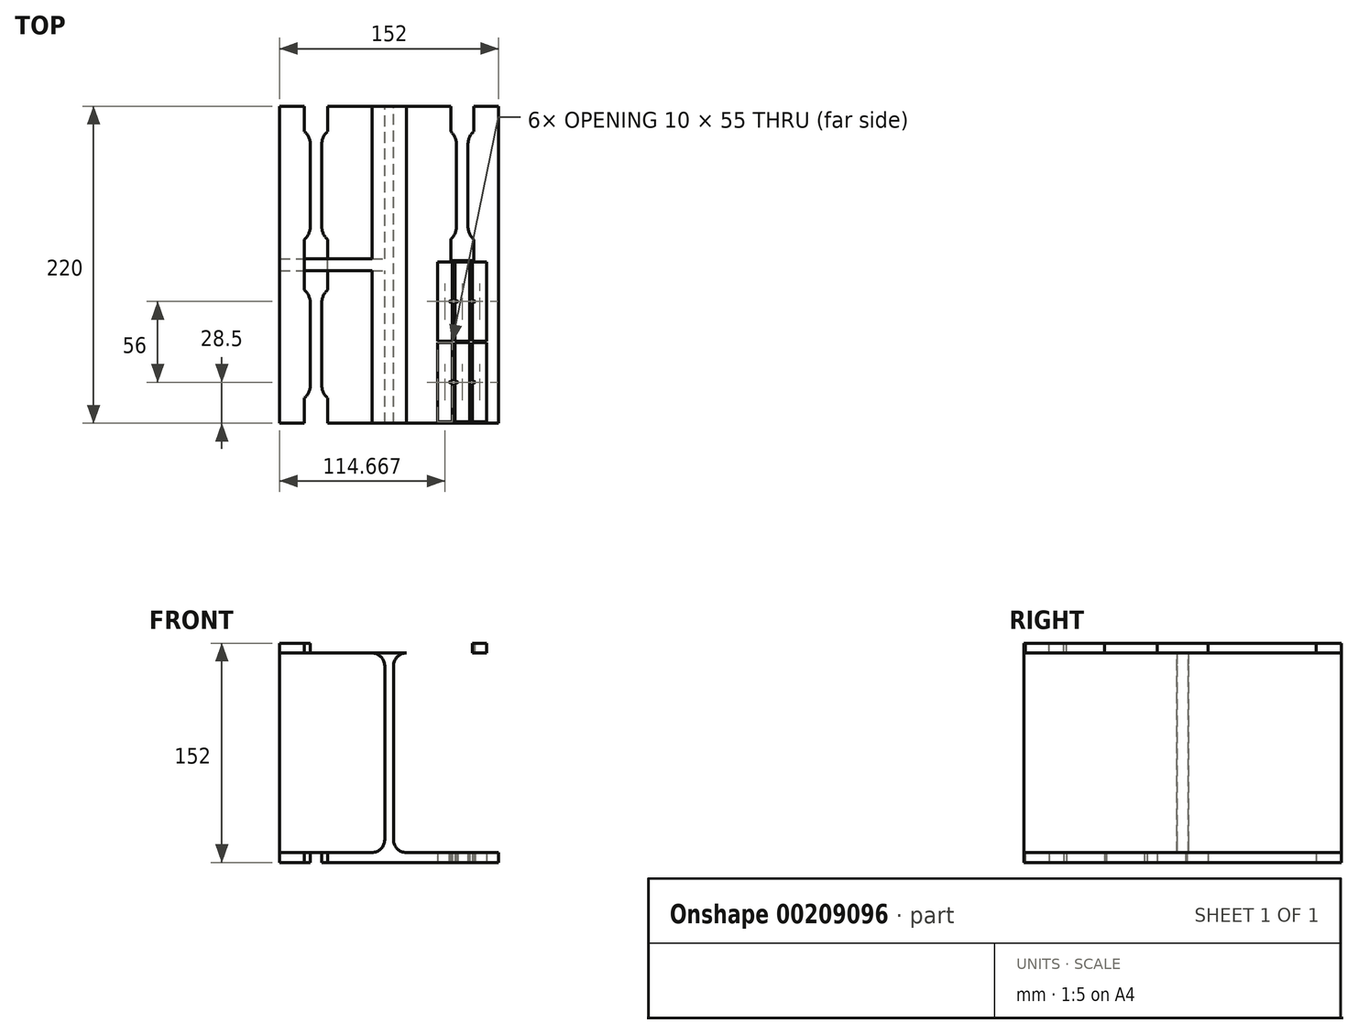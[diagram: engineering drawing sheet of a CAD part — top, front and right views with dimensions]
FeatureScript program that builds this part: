
annotation { "Feature Type Name" : "Feature", "Feature Type Description" : "" }
export const myFeature = defineFeature(function(context is Context, id is Id, definition is map)
    precondition{}
    {
        {
            var Q0;
            Q0=qCreatedBy(makeId("Front.planeOp"),FACE);
            var sketch = newSketch(context, id + "F0", { "sketchPlane" : qUnion([Q0])});
            skLineSegment(sketch, "E0.left", {"start": v(3.05, -60.3) * mm, "end": v(3.05, 60.3) * mm});
            skLineSegment(sketch, "E0.right", {"start": v(-3.05, -60.3) * mm, "end": v(-3.05, 60.3) * mm});
            skPoint(sketch, "E0.middle", {"position": v(0, 0) * mm});
            skLineSegment(sketch, "E1.top", {"start": v(76, 76) * mm, "end": v(-76, 76) * mm});
            skLineSegment(sketch, "E1.left", {"start": v(76, 69.2) * mm, "end": v(76, 76) * mm});
            skLineSegment(sketch, "E1.right", {"start": v(-76, 69.2) * mm, "end": v(-76, 76) * mm});
            skPoint(sketch, "E1.middle", {"position": v(0, 72.6) * mm});
            skPoint(sketch, "E1.middle.positionSnap0", {"position": v(0, 69.2) * mm});
            skPoint(sketch, "E1.centerSnap0", {"position": v(0, 69.2) * mm});
            skLineSegment(sketch, "E2.top", {"start": v(76, -76) * mm, "end": v(-76, -76) * mm});
            skLineSegment(sketch, "E2.left", {"start": v(76, -69.2) * mm, "end": v(76, -76) * mm});
            skLineSegment(sketch, "E2.right", {"start": v(-76, -69.2) * mm, "end": v(-76, -76) * mm});
            skPoint(sketch, "E2.middle", {"position": v(0, -72.6) * mm});
            skLineSegment(sketch, "E3", {"start": v(-76, 69.2) * mm, "end": v(-11.95, 69.2) * mm});
            skLineSegment(sketch, "E4", {"start": v(11.95, 69.2) * mm, "end": v(76, 69.2) * mm});
            skLineSegment(sketch, "E5", {"start": v(11.95, -69.2) * mm, "end": v(76, -69.2) * mm});
            skLineSegment(sketch, "E6", {"start": v(-11.95, -69.2) * mm, "end": v(-76, -69.2) * mm});
            skPoint(sketch, "E7.visualSharp", {"position": v(-3.05, 69.2) * mm});
            skArc(sketch, "E7.filletArc", {"start": v(-3.05, 60.3) * mm, "mid": v(-5.66, 66.6) * mm, "end": v(-11.95, 69.2) * mm});
            skPoint(sketch, "E8.visualSharp", {"position": v(3.05, 69.2) * mm});
            skArc(sketch, "E8.filletArc", {"start": v(11.95, 69.2) * mm, "mid": v(5.66, 66.6) * mm, "end": v(3.05, 60.3) * mm});
            skPoint(sketch, "E9.visualSharp", {"position": v(-3.05, -69.2) * mm});
            skArc(sketch, "E9.filletArc", {"start": v(-11.95, -69.2) * mm, "mid": v(-5.66, -66.6) * mm, "end": v(-3.05, -60.3) * mm});
            skPoint(sketch, "E10.visualSharp", {"position": v(3.05, -69.2) * mm});
            skArc(sketch, "E10.filletArc", {"start": v(3.05, -60.3) * mm, "mid": v(5.66, -66.6) * mm, "end": v(11.95, -69.2) * mm});
            skPoint(sketch, "E11.startSnap0", {"position": v(-5.66, 66.6) * mm});
            skPoint(sketch, "E11.endSnap0", {"position": v(-5.66, 66.6) * mm});
            skPoint(sketch, "E12.startSnap0", {"position": v(-5.66, -66.6) * mm});
            skSolve(sketch);
        }
        {
            var Q0;
            Q0=makeQuery(id+"F0.imprint","IMPRINT",FACE,{"disambiguationData":[TD([[makeQuery(id+"F0.imprint","IMPRINT",EDGE,{"derivedFrom":sQuery(id+"F0.wireOp",EDGE,"E0.left")}),1.0]])]});
            extrude(context, id + "F1", {"entities" : qUnion([Q0]), "depth" : 220 * mm, "symmetric" : true});
        }
        {
            var Q0;
            Q0=makeQuery(id+"F1.opExtrude","SWEPT_FACE",FACE,{"disambiguationData":[OSD([sQuery(id+"F0.wireOp",EDGE,"E1.top")])]});
            var sketch = newSketch(context, id + "F2", { "sketchPlane" : qUnion([Q0])});
            skLineSegment(sketch, "E13.bottom", {"start": v(0, -4) * mm, "end": v(-76, -4) * mm});
            skLineSegment(sketch, "E13.top", {"start": v(0, 4) * mm, "end": v(-76, 4) * mm});
            skLineSegment(sketch, "E13.left", {"start": v(0, -4) * mm, "end": v(0, 4) * mm});
            skLineSegment(sketch, "E13.right", {"start": v(-76, -4) * mm, "end": v(-76, 4) * mm});
            skPoint(sketch, "E13.middle", {"position": v(-38, 0) * mm});
            skSolve(sketch);
        }
        {
            var Q0;
            Q0=makeQuery(id+"F2.imprint","IMPRINT",FACE,{"disambiguationData":[TD([[makeQuery(id+"F2.imprint","IMPRINT",EDGE,{"derivedFrom":sQuery(id+"F2.wireOp",EDGE,"E13.bottom")}),-1.0]])]});
            extrude(context, id + "F3", {"entities" : qUnion([Q0]), "operationType" : NewBodyOperationType.ADD, "oppositeDirection" : true, "depth" : 152 * mm});
        }
        {
            var Q0;
            Q0=makeQuery(id+"F1.opExtrude","SWEPT_FACE",FACE,{"disambiguationData":[OSD([sQuery(id+"F0.wireOp",EDGE,"E1.top")])]});
            var sketch = newSketch(context, id + "F4", { "sketchPlane" : qUnion([Q0])});
            skLineSegment(sketch, "E14.bottom", {"start": v(58.67, 110) * mm, "end": v(42.67, 110) * mm});
            skPoint(sketch, "E14.middle", {"position": v(50.67, 55) * mm});
            skLineSegment(sketch, "E15.left", {"start": v(54.67, 26.5) * mm, "end": v(54.67, 83.5) * mm});
            skLineSegment(sketch, "E15.right", {"start": v(46.67, 26.5) * mm, "end": v(46.67, 83.5) * mm});
            skArc(sketch, "E16", {"start": v(54.67, 83.5) * mm, "mid": v(55.71, 88.4) * mm, "end": v(58.67, 92.44) * mm});
            skArc(sketch, "E17", {"start": v(46.67, 83.5) * mm, "mid": v(45.62, 88.4) * mm, "end": v(42.67, 92.44) * mm});
            skArc(sketch, "E18", {"start": v(54.67, 26.5) * mm, "mid": v(55.71, 21.6) * mm, "end": v(58.67, 17.56) * mm});
            skArc(sketch, "E19", {"start": v(46.67, 26.5) * mm, "mid": v(45.62, 21.6) * mm, "end": v(42.67, 17.56) * mm});
            skLineSegment(sketch, "E20", {"start": v(42.67, 92.44) * mm, "end": v(42.67, 110) * mm});
            skLineSegment(sketch, "E21", {"start": v(58.67, 110) * mm, "end": v(58.67, 92.44) * mm});
            skLineSegment(sketch, "E22", {"start": v(0, 116.32) * mm, "end": v(0, 123.72) * mm});
            skPoint(sketch, "E23.MirrorP", {"position": v(-50.67, 55) * mm});
            skLineSegment(sketch, "E24.MirrorCS", {"start": v(-58.67, 110) * mm, "end": v(-42.67, 110) * mm});
            skLineSegment(sketch, "E25.MirrorCS", {"start": v(-58.67, 110) * mm, "end": v(-58.67, 92.44) * mm});
            skLineSegment(sketch, "E26.MirrorCS", {"start": v(-42.67, 92.44) * mm, "end": v(-42.67, 110) * mm});
            skArc(sketch, "E27.MirrorCS", {"start": v(-54.67, 83.5) * mm, "mid": v(-55.71, 88.4) * mm, "end": v(-58.67, 92.44) * mm});
            skArc(sketch, "E28.MirrorCS", {"start": v(-46.67, 83.5) * mm, "mid": v(-45.62, 88.4) * mm, "end": v(-42.67, 92.44) * mm});
            skLineSegment(sketch, "E29.MirrorCS", {"start": v(-54.67, 26.5) * mm, "end": v(-54.67, 83.5) * mm});
            skLineSegment(sketch, "E30.MirrorCS", {"start": v(-46.67, 26.5) * mm, "end": v(-46.67, 83.5) * mm});
            skArc(sketch, "E31.MirrorCS", {"start": v(-54.67, 26.5) * mm, "mid": v(-55.71, 21.6) * mm, "end": v(-58.67, 17.56) * mm});
            skArc(sketch, "E32.MirrorCS", {"start": v(-46.67, 26.5) * mm, "mid": v(-45.62, 21.6) * mm, "end": v(-42.67, 17.56) * mm});
            skLineSegment(sketch, "E33.MirrorCS", {"start": v(-58.67, 0) * mm, "end": v(-58.67, 17.56) * mm});
            skLineSegment(sketch, "E34.MirrorCS", {"start": v(-58.67, 0) * mm, "end": v(-42.67, 0) * mm});
            skLineSegment(sketch, "E35.MirrorCS", {"start": v(-42.67, 17.56) * mm, "end": v(-42.67, 0) * mm});
            skPoint(sketch, "E36.MirrorP", {"position": v(-50.67, -55) * mm});
            skLineSegment(sketch, "E37.MirrorCS", {"start": v(-58.67, -110) * mm, "end": v(-42.67, -110) * mm});
            skLineSegment(sketch, "E38.MirrorCS", {"start": v(-42.67, -92.44) * mm, "end": v(-42.67, -110) * mm});
            skLineSegment(sketch, "E39.MirrorCS", {"start": v(-58.67, -110) * mm, "end": v(-58.67, -92.44) * mm});
            skArc(sketch, "E40.MirrorCS", {"start": v(-46.67, -83.5) * mm, "mid": v(-45.62, -88.4) * mm, "end": v(-42.67, -92.44) * mm});
            skArc(sketch, "E41.MirrorCS", {"start": v(-54.67, -83.5) * mm, "mid": v(-55.71, -88.4) * mm, "end": v(-58.67, -92.44) * mm});
            skLineSegment(sketch, "E42.MirrorCS", {"start": v(-46.67, -26.5) * mm, "end": v(-46.67, -83.5) * mm});
            skLineSegment(sketch, "E43.MirrorCS", {"start": v(-54.67, -26.5) * mm, "end": v(-54.67, -83.5) * mm});
            skArc(sketch, "E44.MirrorCS", {"start": v(-46.67, -26.5) * mm, "mid": v(-45.62, -21.6) * mm, "end": v(-42.67, -17.56) * mm});
            skArc(sketch, "E45.MirrorCS", {"start": v(-54.67, -26.5) * mm, "mid": v(-55.71, -21.6) * mm, "end": v(-58.67, -17.56) * mm});
            skLineSegment(sketch, "E46.MirrorCS", {"start": v(-42.67, -17.56) * mm, "end": v(-42.67, 0) * mm});
            skLineSegment(sketch, "E47.MirrorCS", {"start": v(-58.67, 0) * mm, "end": v(-58.67, -17.56) * mm});
            skLineSegment(sketch, "E48.bottom", {"start": v(55.67, 2) * mm, "end": v(45.67, 2) * mm});
            skLineSegment(sketch, "E48.top", {"start": v(55.67, -53) * mm, "end": v(45.67, -53) * mm});
            skLineSegment(sketch, "E48.left", {"start": v(55.67, 2) * mm, "end": v(55.67, -53) * mm});
            skPoint(sketch, "E48.middle", {"position": v(50.67, -25.5) * mm});
            skLineSegment(sketch, "E49.top", {"start": v(58.67, 3) * mm, "end": v(42.67, 3) * mm});
            skLineSegment(sketch, "E49.left", {"start": v(58.67, 17.56) * mm, "end": v(58.67, 3) * mm});
            skLineSegment(sketch, "E49.right", {"start": v(42.67, 17.56) * mm, "end": v(42.67, 3) * mm});
            skPoint(sketch, "E49.middle", {"position": v(50.67, 10.28) * mm});
            skLineSegment(sketch, "E50", {"start": v(47.51, -25.27) * mm, "end": v(45.67, -24.5) * mm});
            skLineSegment(sketch, "E51", {"start": v(47.51, -25.73) * mm, "end": v(45.67, -26.5) * mm});
            skLineSegment(sketch, "E52", {"start": v(42.27, -25.5) * mm, "end": v(40.71, -25.5) * mm});
            skPoint(sketch, "E52.startSnap0", {"position": v(45.67, -25.5) * mm});
            skPoint(sketch, "E53.visualSharp", {"position": v(48.07, -25.5) * mm});
            skArc(sketch, "E53.filletArc", {"start": v(47.51, -25.73) * mm, "mid": v(47.67, -25.5) * mm, "end": v(47.51, -25.27) * mm});
            skLineSegment(sketch, "E54", {"start": v(56.67, -9.9) * mm, "end": v(56.67, -20.52) * mm});
            skLineSegment(sketch, "E55", {"start": v(50.67, -17.9) * mm, "end": v(50.67, -13.5) * mm});
            skLineSegment(sketch, "E56.MirrorCS", {"start": v(44.67, -9.9) * mm, "end": v(44.67, -20.52) * mm});
            skLineSegment(sketch, "E57.MirrorCS", {"start": v(57.67, 2) * mm, "end": v(67.67, 2) * mm});
            skPoint(sketch, "E58.MirrorP", {"position": v(62.67, -25.5) * mm});
            skLineSegment(sketch, "E59.MirrorCS", {"start": v(57.67, -53) * mm, "end": v(67.67, -53) * mm});
            skLineSegment(sketch, "E60.MirrorCS", {"start": v(67.67, 2) * mm, "end": v(67.67, -53) * mm});
            skArc(sketch, "E61.MirrorCS", {"start": v(41.82, -25.73) * mm, "mid": v(41.67, -25.5) * mm, "end": v(41.82, -25.27) * mm});
            skLineSegment(sketch, "E62.MirrorCS", {"start": v(41.82, -25.27) * mm, "end": v(43.67, -24.5) * mm});
            skLineSegment(sketch, "E63.MirrorCS", {"start": v(41.82, -25.73) * mm, "end": v(43.67, -26.5) * mm});
            skLineSegment(sketch, "E64.MirrorCS", {"start": v(33.67, 2) * mm, "end": v(43.67, 2) * mm});
            skLineSegment(sketch, "E65.MirrorCS", {"start": v(38.67, -17.9) * mm, "end": v(38.67, -13.5) * mm});
            skPoint(sketch, "E66.MirrorP", {"position": v(38.67, -25.5) * mm});
            skPoint(sketch, "E67.MirrorP", {"position": v(43.67, -25.5) * mm});
            skLineSegment(sketch, "E68.MirrorCS", {"start": v(33.67, 2) * mm, "end": v(33.67, -53) * mm});
            skLineSegment(sketch, "E69.MirrorCS", {"start": v(33.67, -53) * mm, "end": v(43.67, -53) * mm});
            skPoint(sketch, "E70.MirrorP", {"position": v(41.26, -25.5) * mm});
            skLineSegment(sketch, "E71", {"start": v(62.67, -21.23) * mm, "end": v(62.67, -17.56) * mm});
            skArc(sketch, "E72.MirrorCS", {"start": v(59.51, -25.73) * mm, "mid": v(59.67, -25.5) * mm, "end": v(59.51, -25.27) * mm});
            skLineSegment(sketch, "E73.MirrorCS", {"start": v(59.51, -25.73) * mm, "end": v(57.67, -26.5) * mm});
            skLineSegment(sketch, "E74.MirrorCS", {"start": v(59.51, -25.27) * mm, "end": v(57.67, -24.5) * mm});
            skPoint(sketch, "E75.MirrorP", {"position": v(57.67, -25.5) * mm});
            skPoint(sketch, "E76.MirrorP", {"position": v(60.07, -25.5) * mm});
            skLineSegment(sketch, "E77", {"start": v(43.67, 2) * mm, "end": v(43.67, -24.5) * mm});
            skLineSegment(sketch, "E78", {"start": v(43.67, -26.5) * mm, "end": v(43.67, -53) * mm});
            skLineSegment(sketch, "E79", {"start": v(45.67, -53) * mm, "end": v(45.67, -26.5) * mm});
            skLineSegment(sketch, "E80", {"start": v(45.67, -24.5) * mm, "end": v(45.67, 2) * mm});
            skLineSegment(sketch, "E81", {"start": v(57.67, 2) * mm, "end": v(57.67, -24.5) * mm});
            skLineSegment(sketch, "E82", {"start": v(57.67, -26.5) * mm, "end": v(57.67, -53) * mm});
            skLineSegment(sketch, "E83", {"start": v(42.84, -53.5) * mm, "end": v(60.64, -53.5) * mm});
            skArc(sketch, "E84.MirrorCS", {"start": v(41.82, -81.27) * mm, "mid": v(41.67, -81.5) * mm, "end": v(41.82, -81.73) * mm});
            skLineSegment(sketch, "E85.MirrorCS", {"start": v(41.82, -81.73) * mm, "end": v(43.67, -82.5) * mm});
            skArc(sketch, "E86.MirrorCS", {"start": v(59.51, -81.27) * mm, "mid": v(59.67, -81.5) * mm, "end": v(59.51, -81.73) * mm});
            skLineSegment(sketch, "E87.MirrorCS", {"start": v(42.27, -81.5) * mm, "end": v(40.71, -81.5) * mm});
            skLineSegment(sketch, "E88.MirrorCS", {"start": v(41.82, -81.27) * mm, "end": v(43.67, -80.5) * mm});
            skLineSegment(sketch, "E89.MirrorCS", {"start": v(59.51, -81.73) * mm, "end": v(57.67, -82.5) * mm});
            skLineSegment(sketch, "E90.MirrorCS", {"start": v(59.51, -81.27) * mm, "end": v(57.67, -80.5) * mm});
            skLineSegment(sketch, "E91.MirrorCS", {"start": v(47.51, -81.73) * mm, "end": v(45.67, -82.5) * mm});
            skArc(sketch, "E92.MirrorCS", {"start": v(47.51, -81.27) * mm, "mid": v(47.67, -81.5) * mm, "end": v(47.51, -81.73) * mm});
            skLineSegment(sketch, "E93.MirrorCS", {"start": v(47.51, -81.27) * mm, "end": v(45.67, -80.5) * mm});
            skLineSegment(sketch, "E94.MirrorCS", {"start": v(62.67, -85.77) * mm, "end": v(62.67, -89.44) * mm});
            skPoint(sketch, "E95.MirrorP", {"position": v(43.67, -81.5) * mm});
            skPoint(sketch, "E96.MirrorP", {"position": v(41.26, -81.5) * mm});
            skLineSegment(sketch, "E97.MirrorCS", {"start": v(55.67, -54) * mm, "end": v(45.67, -54) * mm});
            skLineSegment(sketch, "E98.MirrorCS", {"start": v(57.67, -109) * mm, "end": v(67.67, -109) * mm});
            skLineSegment(sketch, "E99.MirrorCS", {"start": v(55.67, -109) * mm, "end": v(45.67, -109) * mm});
            skLineSegment(sketch, "E100.MirrorCS", {"start": v(33.67, -109) * mm, "end": v(43.67, -109) * mm});
            skLineSegment(sketch, "E101.MirrorCS", {"start": v(50.67, -89.1) * mm, "end": v(50.67, -93.5) * mm});
            skLineSegment(sketch, "E102.MirrorCS", {"start": v(38.67, -89.1) * mm, "end": v(38.67, -93.5) * mm});
            skLineSegment(sketch, "E103.MirrorCS", {"start": v(57.67, -109) * mm, "end": v(57.67, -82.5) * mm});
            skLineSegment(sketch, "E104.MirrorCS", {"start": v(56.67, -97.1) * mm, "end": v(56.67, -86.48) * mm});
            skLineSegment(sketch, "E105.MirrorCS", {"start": v(45.67, -82.5) * mm, "end": v(45.67, -109) * mm});
            skLineSegment(sketch, "E106.MirrorCS", {"start": v(44.67, -97.1) * mm, "end": v(44.67, -86.48) * mm});
            skLineSegment(sketch, "E107.MirrorCS", {"start": v(43.67, -109) * mm, "end": v(43.67, -82.5) * mm});
            skPoint(sketch, "E108.MirrorP", {"position": v(48.07, -81.5) * mm});
            skPoint(sketch, "E109.MirrorP", {"position": v(45.67, -81.5) * mm});
            skPoint(sketch, "E110.MirrorP", {"position": v(38.67, -81.5) * mm});
            skPoint(sketch, "E111.MirrorP", {"position": v(62.67, -81.5) * mm});
            skPoint(sketch, "E112.MirrorP", {"position": v(60.07, -81.5) * mm});
            skPoint(sketch, "E113.MirrorP", {"position": v(57.67, -81.5) * mm});
            skPoint(sketch, "E114.MirrorP", {"position": v(50.67, -81.5) * mm});
            skLineSegment(sketch, "E115.MirrorCS", {"start": v(67.67, -109) * mm, "end": v(67.67, -54) * mm});
            skLineSegment(sketch, "E116.MirrorCS", {"start": v(57.67, -80.5) * mm, "end": v(57.67, -54) * mm});
            skLineSegment(sketch, "E117.MirrorCS", {"start": v(55.67, -109) * mm, "end": v(55.67, -54) * mm});
            skLineSegment(sketch, "E118.MirrorCS", {"start": v(45.67, -54) * mm, "end": v(45.67, -80.5) * mm});
            skLineSegment(sketch, "E119.MirrorCS", {"start": v(43.67, -80.5) * mm, "end": v(43.67, -54) * mm});
            skLineSegment(sketch, "E120.MirrorCS", {"start": v(33.67, -109) * mm, "end": v(33.67, -54) * mm});
            skLineSegment(sketch, "E121.MirrorCS", {"start": v(33.67, -54) * mm, "end": v(43.67, -54) * mm});
            skLineSegment(sketch, "E122.MirrorCS", {"start": v(57.67, -54) * mm, "end": v(67.67, -54) * mm});
            skSolve(sketch);
        }
        {
            var Q0;
            Q0=makeQuery(id+"F4.imprint","IMPRINT",FACE,{"disambiguationData":[TD([[makeQuery(id+"F4.imprint","IMPRINT",EDGE,{"derivedFrom":sQuery(id+"F4.wireOp",EDGE,"E24.MirrorCS")}),1.0]])]});
            var Q1;
            Q1=makeQuery(id+"F4.imprint","IMPRINT",FACE,{"disambiguationData":[TD([[makeQuery(id+"F4.imprint","IMPRINT",EDGE,{"derivedFrom":sQuery(id+"F4.wireOp",EDGE,"E34.MirrorCS")}),-1.0]])]});
            var Q2;
            Q2=makeQuery(id+"F4.imprint","IMPRINT",FACE,{"disambiguationData":[TD([[makeQuery(id+"F4.imprint","IMPRINT",EDGE,{"derivedFrom":sQuery(id+"F4.wireOp",EDGE,"E14.bottom")}),1.0]])]});
            var Q3;
            {var subQ0=sQuery(id+"F4.wireOp",EDGE,"E62.MirrorCS");Q3=makeQuery(id+"F4.imprint","IMPRINT",FACE,{"disambiguationData":[TD([[makeQuery(id+"F4.imprint","IMPRINT",EDGE,{"derivedFrom":subQ0}),1.0]])]});}
            var Q4;
            Q4=makeQuery(id+"F4.imprint","IMPRINT",FACE,{"disambiguationData":[TD([[makeQuery(id+"F4.imprint","IMPRINT",EDGE,{"derivedFrom":sQuery(id+"F4.wireOp",EDGE,"E48.bottom")}),1.0]])]});
            var Q5;
            Q5=makeQuery(id+"F4.imprint","IMPRINT",FACE,{"disambiguationData":[TD([[makeQuery(id+"F4.imprint","IMPRINT",EDGE,{"derivedFrom":sQuery(id+"F4.wireOp",EDGE,"E57.MirrorCS")}),-1.0]])]});
            var Q6;
            {var subQ1=sQuery(id+"F4.wireOp",EDGE,"E85.MirrorCS");Q6=makeQuery(id+"F4.imprint","IMPRINT",FACE,{"disambiguationData":[TD([[makeQuery(id+"F4.imprint","IMPRINT",EDGE,{"derivedFrom":subQ1}),-1.0]])]});}
            var Q7;
            Q7=makeQuery(id+"F4.imprint","IMPRINT",FACE,{"disambiguationData":[TD([[makeQuery(id+"F4.imprint","IMPRINT",EDGE,{"derivedFrom":sQuery(id+"F4.wireOp",EDGE,"E91.MirrorCS")}),1.0]])]});
            var Q8;
            Q8=makeQuery(id+"F4.imprint","IMPRINT",FACE,{"disambiguationData":[TD([[makeQuery(id+"F4.imprint","IMPRINT",EDGE,{"derivedFrom":sQuery(id+"F4.wireOp",EDGE,"E86.MirrorCS")}),1.0]])]});
            extrude(context, id + "F5", {"entities" : qUnion([Q0, Q1, Q2, Q3, Q4, Q5, Q6, Q7, Q8]), "operationType" : NewBodyOperationType.REMOVE, "oppositeDirection" : true, "depth" : 6.8 * mm});
        }
        {
            var Q0;
            Q0=makeQuery(id+"F1.opExtrude","SWEPT_FACE",FACE,{"disambiguationData":[OSD([sQuery(id+"F0.wireOp",EDGE,"E2.top")])]});
            var sketch = newSketch(context, id + "F6", { "sketchPlane" : qUnion([Q0])});
            skLineSegment(sketch, "E123.bottom", {"start": v(-42.67, 110) * mm, "end": v(-58.67, 110) * mm});
            skLineSegment(sketch, "E123.top", {"start": v(-42.67, 0) * mm, "end": v(-58.67, 0) * mm});
            skPoint(sketch, "E123.middle", {"position": v(-50.67, 55) * mm});
            skLineSegment(sketch, "E124.left", {"start": v(-46.67, 26.5) * mm, "end": v(-46.67, 83.5) * mm});
            skLineSegment(sketch, "E124.right", {"start": v(-54.67, 26.5) * mm, "end": v(-54.67, 83.5) * mm});
            skArc(sketch, "E125", {"start": v(-46.67, 83.5) * mm, "mid": v(-45.62, 88.4) * mm, "end": v(-42.67, 92.44) * mm});
            skArc(sketch, "E126", {"start": v(-54.67, 83.5) * mm, "mid": v(-55.71, 88.4) * mm, "end": v(-58.67, 92.44) * mm});
            skArc(sketch, "E127", {"start": v(-46.67, 26.5) * mm, "mid": v(-45.62, 21.6) * mm, "end": v(-42.67, 17.56) * mm});
            skArc(sketch, "E128", {"start": v(-54.67, 26.5) * mm, "mid": v(-55.71, 21.6) * mm, "end": v(-58.67, 17.56) * mm});
            skLineSegment(sketch, "E129", {"start": v(-58.67, 110) * mm, "end": v(-58.67, 92.44) * mm});
            skLineSegment(sketch, "E130", {"start": v(-42.67, 110) * mm, "end": v(-42.67, 92.44) * mm});
            skLineSegment(sketch, "E131", {"start": v(-42.67, 17.56) * mm, "end": v(-42.67, 0) * mm});
            skLineSegment(sketch, "E132", {"start": v(-58.67, 0) * mm, "end": v(-58.67, 17.56) * mm});
            skArc(sketch, "E133.MirrorCS", {"start": v(-46.67, -26.5) * mm, "mid": v(-45.62, -21.6) * mm, "end": v(-42.67, -17.56) * mm});
            skArc(sketch, "E134.MirrorCS", {"start": v(-46.67, -83.5) * mm, "mid": v(-45.62, -88.4) * mm, "end": v(-42.67, -92.44) * mm});
            skArc(sketch, "E135.MirrorCS", {"start": v(-54.67, -83.5) * mm, "mid": v(-55.71, -88.4) * mm, "end": v(-58.67, -92.44) * mm});
            skArc(sketch, "E136.MirrorCS", {"start": v(-54.67, -26.5) * mm, "mid": v(-55.71, -21.6) * mm, "end": v(-58.67, -17.56) * mm});
            skPoint(sketch, "E137.MirrorP", {"position": v(-50.67, -55) * mm});
            skLineSegment(sketch, "E138.MirrorCS", {"start": v(-42.67, -110) * mm, "end": v(-58.67, -110) * mm});
            skLineSegment(sketch, "E139.MirrorCS", {"start": v(-42.67, -110) * mm, "end": v(-42.67, -92.44) * mm});
            skLineSegment(sketch, "E140.MirrorCS", {"start": v(-58.67, -110) * mm, "end": v(-58.67, -92.44) * mm});
            skLineSegment(sketch, "E141.MirrorCS", {"start": v(-46.67, -26.5) * mm, "end": v(-46.67, -83.5) * mm});
            skLineSegment(sketch, "E142.MirrorCS", {"start": v(-54.67, -26.5) * mm, "end": v(-54.67, -83.5) * mm});
            skLineSegment(sketch, "E143.MirrorCS", {"start": v(-42.67, -17.56) * mm, "end": v(-42.67, 0) * mm});
            skLineSegment(sketch, "E144.MirrorCS", {"start": v(-58.67, 0) * mm, "end": v(-58.67, -17.56) * mm});
            skLineSegment(sketch, "E145", {"start": v(0, -15.92) * mm, "end": v(0, -24.69) * mm});
            skPoint(sketch, "E146.MirrorP", {"position": v(50.67, -55) * mm});
            skArc(sketch, "E147.MirrorCS", {"start": v(46.67, -26.5) * mm, "mid": v(45.62, -21.6) * mm, "end": v(42.67, -17.56) * mm});
            skArc(sketch, "E148.MirrorCS", {"start": v(54.67, -26.5) * mm, "mid": v(55.71, -21.6) * mm, "end": v(58.67, -17.56) * mm});
            skLineSegment(sketch, "E149.MirrorCS", {"start": v(54.67, -26.5) * mm, "end": v(54.67, -83.5) * mm});
            skArc(sketch, "E150.MirrorCS", {"start": v(46.67, -83.5) * mm, "mid": v(45.62, -88.4) * mm, "end": v(42.67, -92.44) * mm});
            skArc(sketch, "E151.MirrorCS", {"start": v(54.67, -83.5) * mm, "mid": v(55.71, -88.4) * mm, "end": v(58.67, -92.44) * mm});
            skLineSegment(sketch, "E152.MirrorCS", {"start": v(42.67, -110) * mm, "end": v(42.67, -92.44) * mm});
            skLineSegment(sketch, "E153.MirrorCS", {"start": v(58.67, -110) * mm, "end": v(58.67, -92.44) * mm});
            skLineSegment(sketch, "E154.MirrorCS", {"start": v(46.67, -26.5) * mm, "end": v(46.67, -83.5) * mm});
            skLineSegment(sketch, "E155.MirrorCS", {"start": v(42.67, -110) * mm, "end": v(58.67, -110) * mm});
            skLineSegment(sketch, "E156.bottom", {"start": v(55.67, -2) * mm, "end": v(45.67, -2) * mm});
            skLineSegment(sketch, "E156.top", {"start": v(55.67, 53) * mm, "end": v(45.67, 53) * mm});
            skLineSegment(sketch, "E156.left", {"start": v(55.67, -2) * mm, "end": v(55.67, 53) * mm});
            skPoint(sketch, "E156.middle", {"position": v(50.67, 25.5) * mm});
            skLineSegment(sketch, "E157.top", {"start": v(58.67, -3) * mm, "end": v(42.67, -3) * mm});
            skLineSegment(sketch, "E157.left", {"start": v(58.67, -17.56) * mm, "end": v(58.67, -3) * mm});
            skLineSegment(sketch, "E157.right", {"start": v(42.67, -17.56) * mm, "end": v(42.67, -3) * mm});
            skPoint(sketch, "E157.middle", {"position": v(50.67, -10.28) * mm});
            skLineSegment(sketch, "E158", {"start": v(45.67, 26.5) * mm, "end": v(47.51, 25.73) * mm});
            skLineSegment(sketch, "E159", {"start": v(47.51, 25.27) * mm, "end": v(45.67, 24.5) * mm});
            skLineSegment(sketch, "E160", {"start": v(43.24, 25.5) * mm, "end": v(40.26, 25.5) * mm});
            skPoint(sketch, "E160.startSnap0", {"position": v(45.67, 25.5) * mm});
            skPoint(sketch, "E160.endSnap0", {"position": v(45.67, 25.5) * mm});
            skPoint(sketch, "E161.visualSharp", {"position": v(48.07, 25.5) * mm});
            skArc(sketch, "E161.filletArc", {"start": v(47.51, 25.27) * mm, "mid": v(47.67, 25.5) * mm, "end": v(47.51, 25.73) * mm});
            skLineSegment(sketch, "E162", {"start": v(56.67, 28.54) * mm, "end": v(56.67, 21.7) * mm});
            skLineSegment(sketch, "E163", {"start": v(50.67, 30.56) * mm, "end": v(50.67, 34.07) * mm});
            skLineSegment(sketch, "E164.MirrorCS", {"start": v(44.67, 28.54) * mm, "end": v(44.67, 21.7) * mm});
            skLineSegment(sketch, "E165.MirrorCS", {"start": v(57.67, 53) * mm, "end": v(67.67, 53) * mm});
            skPoint(sketch, "E166.MirrorP", {"position": v(62.67, 25.5) * mm});
            skLineSegment(sketch, "E167.MirrorCS", {"start": v(57.67, -2) * mm, "end": v(67.67, -2) * mm});
            skLineSegment(sketch, "E168.MirrorCS", {"start": v(67.67, -2) * mm, "end": v(67.67, 53) * mm});
            skArc(sketch, "E169.MirrorCS", {"start": v(41.82, 25.27) * mm, "mid": v(41.67, 25.5) * mm, "end": v(41.82, 25.73) * mm});
            skLineSegment(sketch, "E170.MirrorCS", {"start": v(43.67, 26.5) * mm, "end": v(41.82, 25.73) * mm});
            skLineSegment(sketch, "E171.MirrorCS", {"start": v(41.82, 25.27) * mm, "end": v(43.67, 24.5) * mm});
            skPoint(sketch, "E172.MirrorP", {"position": v(43.67, 25.5) * mm});
            skLineSegment(sketch, "E173.MirrorCS", {"start": v(33.67, 53) * mm, "end": v(43.67, 53) * mm});
            skPoint(sketch, "E174.MirrorP", {"position": v(38.67, 25.5) * mm});
            skPoint(sketch, "E175.MirrorP", {"position": v(41.26, 25.5) * mm});
            skLineSegment(sketch, "E176.MirrorCS", {"start": v(33.67, -2) * mm, "end": v(33.67, 53) * mm});
            skLineSegment(sketch, "E177.MirrorCS", {"start": v(33.67, -2) * mm, "end": v(43.67, -2) * mm});
            skLineSegment(sketch, "E178", {"start": v(62.67, 28.91) * mm, "end": v(62.67, 34.52) * mm});
            skArc(sketch, "E179.MirrorCS", {"start": v(59.51, 25.27) * mm, "mid": v(59.67, 25.5) * mm, "end": v(59.51, 25.73) * mm});
            skPoint(sketch, "E180.MirrorP", {"position": v(57.67, 25.5) * mm});
            skLineSegment(sketch, "E181.MirrorCS", {"start": v(59.51, 25.27) * mm, "end": v(57.67, 24.5) * mm});
            skLineSegment(sketch, "E182.MirrorCS", {"start": v(57.67, 26.5) * mm, "end": v(59.51, 25.73) * mm});
            skPoint(sketch, "E183.MirrorP", {"position": v(60.07, 25.5) * mm});
            skLineSegment(sketch, "E184", {"start": v(43.67, 53) * mm, "end": v(43.67, 26.5) * mm});
            skLineSegment(sketch, "E185", {"start": v(43.67, 24.5) * mm, "end": v(43.67, -2) * mm});
            skLineSegment(sketch, "E186", {"start": v(45.67, -2) * mm, "end": v(45.67, 24.5) * mm});
            skLineSegment(sketch, "E187", {"start": v(45.67, 26.5) * mm, "end": v(45.67, 53) * mm});
            skLineSegment(sketch, "E188", {"start": v(57.67, 53) * mm, "end": v(57.67, 26.5) * mm});
            skLineSegment(sketch, "E189", {"start": v(57.67, 24.5) * mm, "end": v(57.67, -2) * mm});
            skLineSegment(sketch, "E190", {"start": v(40.2, 53.5) * mm, "end": v(61.92, 53.5) * mm});
            skLineSegment(sketch, "E191.MirrorCS", {"start": v(43.67, 80.5) * mm, "end": v(41.82, 81.27) * mm});
            skArc(sketch, "E192.MirrorCS", {"start": v(41.82, 81.73) * mm, "mid": v(41.67, 81.5) * mm, "end": v(41.82, 81.27) * mm});
            skLineSegment(sketch, "E193.MirrorCS", {"start": v(43.24, 81.5) * mm, "end": v(40.26, 81.5) * mm});
            skLineSegment(sketch, "E194.MirrorCS", {"start": v(47.51, 81.73) * mm, "end": v(45.67, 82.5) * mm});
            skLineSegment(sketch, "E195.MirrorCS", {"start": v(41.82, 81.73) * mm, "end": v(43.67, 82.5) * mm});
            skLineSegment(sketch, "E196.MirrorCS", {"start": v(45.67, 80.5) * mm, "end": v(47.51, 81.27) * mm});
            skLineSegment(sketch, "E197.MirrorCS", {"start": v(57.67, 80.5) * mm, "end": v(59.51, 81.27) * mm});
            skArc(sketch, "E198.MirrorCS", {"start": v(59.51, 81.73) * mm, "mid": v(59.67, 81.5) * mm, "end": v(59.51, 81.27) * mm});
            skArc(sketch, "E199.MirrorCS", {"start": v(47.51, 81.73) * mm, "mid": v(47.67, 81.5) * mm, "end": v(47.51, 81.27) * mm});
            skLineSegment(sketch, "E200.MirrorCS", {"start": v(59.51, 81.73) * mm, "end": v(57.67, 82.5) * mm});
            skPoint(sketch, "E201.MirrorP", {"position": v(45.67, 81.5) * mm});
            skPoint(sketch, "E202.MirrorP", {"position": v(43.67, 81.5) * mm});
            skPoint(sketch, "E203.MirrorP", {"position": v(57.67, 81.5) * mm});
            skPoint(sketch, "E204.MirrorP", {"position": v(41.26, 81.5) * mm});
            skLineSegment(sketch, "E205.MirrorCS", {"start": v(57.67, 54) * mm, "end": v(67.67, 54) * mm});
            skLineSegment(sketch, "E206.MirrorCS", {"start": v(33.67, 54) * mm, "end": v(43.67, 54) * mm});
            skLineSegment(sketch, "E207.MirrorCS", {"start": v(45.67, 80.5) * mm, "end": v(45.67, 54) * mm});
            skPoint(sketch, "E208.MirrorP", {"position": v(62.67, 81.5) * mm});
            skPoint(sketch, "E209.MirrorP", {"position": v(60.07, 81.5) * mm});
            skPoint(sketch, "E210.MirrorP", {"position": v(50.67, 81.5) * mm});
            skPoint(sketch, "E211.MirrorP", {"position": v(38.67, 81.5) * mm});
            skLineSegment(sketch, "E212.MirrorCS", {"start": v(67.67, 109) * mm, "end": v(67.67, 54) * mm});
            skLineSegment(sketch, "E213.MirrorCS", {"start": v(55.67, 109) * mm, "end": v(55.67, 54) * mm});
            skLineSegment(sketch, "E214.MirrorCS", {"start": v(33.67, 109) * mm, "end": v(33.67, 54) * mm});
            skLineSegment(sketch, "E215.MirrorCS", {"start": v(55.67, 109) * mm, "end": v(45.67, 109) * mm});
            skLineSegment(sketch, "E216.MirrorCS", {"start": v(33.67, 109) * mm, "end": v(43.67, 109) * mm});
            skLineSegment(sketch, "E217.MirrorCS", {"start": v(55.67, 54) * mm, "end": v(45.67, 54) * mm});
            skPoint(sketch, "E218.MirrorP", {"position": v(48.07, 81.5) * mm});
            skLineSegment(sketch, "E219.MirrorCS", {"start": v(57.67, 54) * mm, "end": v(57.67, 80.5) * mm});
            skLineSegment(sketch, "E220.MirrorCS", {"start": v(57.67, 109) * mm, "end": v(67.67, 109) * mm});
            skLineSegment(sketch, "E221.MirrorCS", {"start": v(45.67, 109) * mm, "end": v(45.67, 82.5) * mm});
            skLineSegment(sketch, "E222.MirrorCS", {"start": v(43.67, 82.5) * mm, "end": v(43.67, 109) * mm});
            skLineSegment(sketch, "E223.MirrorCS", {"start": v(57.67, 82.5) * mm, "end": v(57.67, 109) * mm});
            skLineSegment(sketch, "E224.MirrorCS", {"start": v(43.67, 54) * mm, "end": v(43.67, 80.5) * mm});
            skSolve(sketch);
        }
        {
            var Q0;
            Q0=makeQuery(id+"F6.imprint","IMPRINT",FACE,{"disambiguationData":[TD([[makeQuery(id+"F6.imprint","IMPRINT",EDGE,{"derivedFrom":sQuery(id+"F6.wireOp",EDGE,"E123.bottom")}),1.0]])]});
            var Q1;
            {var subQ1=sQuery(id+"F6.wireOp",EDGE,"E191.MirrorCS");Q1=makeQuery(id+"F6.imprint","IMPRINT",FACE,{"disambiguationData":[TD([[makeQuery(id+"F6.imprint","IMPRINT",EDGE,{"derivedFrom":subQ1}),1.0]])]});}
            var Q2;
            Q2=makeQuery(id+"F6.imprint","IMPRINT",FACE,{"disambiguationData":[TD([[makeQuery(id+"F6.imprint","IMPRINT",EDGE,{"derivedFrom":sQuery(id+"F6.wireOp",EDGE,"E194.MirrorCS")}),-1.0]])]});
            var Q3;
            Q3=makeQuery(id+"F6.imprint","IMPRINT",FACE,{"disambiguationData":[TD([[makeQuery(id+"F6.imprint","IMPRINT",EDGE,{"derivedFrom":sQuery(id+"F6.wireOp",EDGE,"E197.MirrorCS")}),-1.0]])]});
            var Q4;
            {var subQ0=sQuery(id+"F6.wireOp",EDGE,"E170.MirrorCS");Q4=makeQuery(id+"F6.imprint","IMPRINT",FACE,{"disambiguationData":[TD([[makeQuery(id+"F6.imprint","IMPRINT",EDGE,{"derivedFrom":subQ0}),-1.0]])]});}
            var Q5;
            Q5=makeQuery(id+"F6.imprint","IMPRINT",FACE,{"disambiguationData":[TD([[makeQuery(id+"F6.imprint","IMPRINT",EDGE,{"derivedFrom":sQuery(id+"F6.wireOp",EDGE,"E156.bottom")}),-1.0]])]});
            var Q6;
            Q6=makeQuery(id+"F6.imprint","IMPRINT",FACE,{"disambiguationData":[TD([[makeQuery(id+"F6.imprint","IMPRINT",EDGE,{"derivedFrom":sQuery(id+"F6.wireOp",EDGE,"E165.MirrorCS")}),-1.0]])]});
            var Q7;
            Q7=makeQuery(id+"F6.imprint","IMPRINT",FACE,{"disambiguationData":[TD([[makeQuery(id+"F6.imprint","IMPRINT",EDGE,{"derivedFrom":sQuery(id+"F6.wireOp",EDGE,"E147.MirrorCS")}),-1.0]])]});
            var Q8;
            Q8=makeQuery(id+"F6.imprint","IMPRINT",FACE,{"disambiguationData":[TD([[makeQuery(id+"F6.imprint","IMPRINT",EDGE,{"derivedFrom":sQuery(id+"F6.wireOp",EDGE,"E123.top")}),1.0]])]});
            extrude(context, id + "F7", {"entities" : qUnion([Q0, Q1, Q2, Q3, Q4, Q5, Q6, Q7, Q8]), "operationType" : NewBodyOperationType.REMOVE, "oppositeDirection" : true, "depth" : 6.8 * mm});
        }
    });
